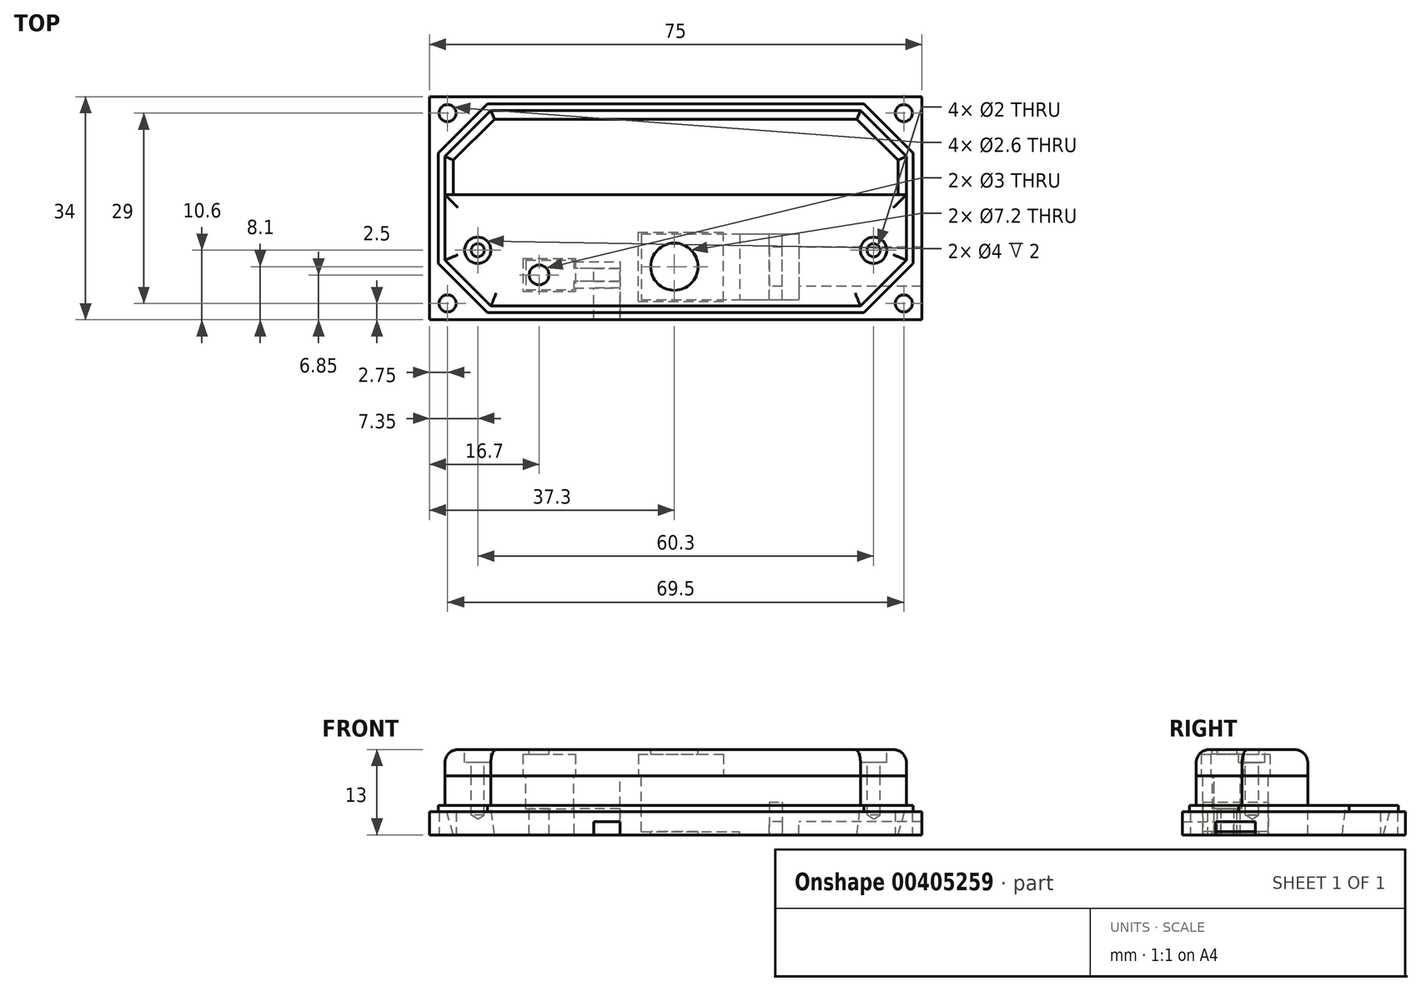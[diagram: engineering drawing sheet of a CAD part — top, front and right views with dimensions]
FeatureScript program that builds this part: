
annotation { "Feature Type Name" : "Feature", "Feature Type Description" : "" }
export const myFeature = defineFeature(function(context is Context, id is Id, definition is map)
    precondition{}
    {
        {
            var Q0;
            Q0=qCreatedBy(makeId("Top.planeOp"),FACE);
            var sketch = newSketch(context, id + "F0", { "sketchPlane" : qUnion([Q0])});
            skLineSegment(sketch, "E0.bottom", {"start": v(37.5, -17) * mm, "end": v(-37.5, -17) * mm});
            skLineSegment(sketch, "E0.top", {"start": v(37.5, 17) * mm, "end": v(-37.5, 17) * mm});
            skLineSegment(sketch, "E0.left", {"start": v(37.5, -17) * mm, "end": v(37.5, 17) * mm});
            skLineSegment(sketch, "E0.right", {"start": v(-37.5, -17) * mm, "end": v(-37.5, 17) * mm});
            skPoint(sketch, "E0.middle", {"position": v(0, 0) * mm});
            skLineSegment(sketch, "E1.bottom", {"start": v(-28.65, 15.9) * mm, "end": v(28.65, 15.9) * mm, "construction": true});
            skLineSegment(sketch, "E1.top", {"start": v(-28.65, -15.9) * mm, "end": v(28.65, -15.9) * mm, "construction": true});
            skLineSegment(sketch, "E1.left", {"start": v(-36.15, 8.4) * mm, "end": v(-36.15, -8.4) * mm, "construction": true});
            skLineSegment(sketch, "E1.right", {"start": v(36.15, 8.4) * mm, "end": v(36.15, -8.4) * mm, "construction": true});
            skLineSegment(sketch, "E2", {"start": v(-36.15, 8.4) * mm, "end": v(-28.65, 15.9) * mm, "construction": true});
            skLineSegment(sketch, "E3", {"start": v(28.65, 15.9) * mm, "end": v(36.15, 8.4) * mm, "construction": true});
            skLineSegment(sketch, "E4", {"start": v(36.15, -8.4) * mm, "end": v(28.65, -15.9) * mm, "construction": true});
            skLineSegment(sketch, "E5", {"start": v(-36.15, -8.4) * mm, "end": v(-28.65, -15.9) * mm, "construction": true});
            skCircle(sketch, "E6", {"center": v(-34.75, 14.5) * mm, "radius": 1.3 * mm});
            skCircle(sketch, "E7", {"center": v(34.75, 14.5) * mm, "radius": 1.3 * mm});
            skCircle(sketch, "E8", {"center": v(-34.75, -14.5) * mm, "radius": 1.3 * mm});
            skCircle(sketch, "E9", {"center": v(34.75, -14.5) * mm, "radius": 1.3 * mm});
            skLineSegment(sketch, "E10", {"start": v(0, -47.1) * mm, "end": v(0, -78.86) * mm, "construction": true});
            skSolve(sketch);
        }
        {
            var Q0;
            Q0=qSketchRegion(id+"F0",true);
            extrude(context, id + "F1", {"entities" : qUnion([Q0]), "depth" : 3.5 * mm});
        }
        {
            var Q0;
            Q0=makeQuery(id+"F1.opExtrude","CAP_FACE",FACE,{"disambiguationData":[OSD([sQuery(id+"F0.wireOp",EDGE,"E0.bottom"),sQuery(id+"F0.wireOp",EDGE,"E0.top"),sQuery(id+"F0.wireOp",EDGE,"E0.left"),sQuery(id+"F0.wireOp",EDGE,"E0.right"),sQuery(id+"F0.wireOp",EDGE,"E6"),sQuery(id+"F0.wireOp",EDGE,"E7"),sQuery(id+"F0.wireOp",EDGE,"E8"),sQuery(id+"F0.wireOp",EDGE,"E9")])],"isStart":false});
            var sketch = newSketch(context, id + "F2", { "sketchPlane" : qUnion([Q0])});
            skLineSegment(sketch, "E11.bottom", {"start": v(-28.65, 15.9) * mm, "end": v(28.65, 15.9) * mm});
            skLineSegment(sketch, "E11.top", {"start": v(-28.65, -15.9) * mm, "end": v(28.65, -15.9) * mm});
            skLineSegment(sketch, "E11.left", {"start": v(-36.15, 8.4) * mm, "end": v(-36.15, -8.4) * mm});
            skLineSegment(sketch, "E11.right", {"start": v(36.15, 8.4) * mm, "end": v(36.15, -8.4) * mm});
            skLineSegment(sketch, "E12", {"start": v(-36.15, 8.4) * mm, "end": v(-28.65, 15.9) * mm});
            skLineSegment(sketch, "E13", {"start": v(28.65, 15.9) * mm, "end": v(36.15, 8.4) * mm});
            skLineSegment(sketch, "E14", {"start": v(36.15, -8.4) * mm, "end": v(28.65, -15.9) * mm});
            skLineSegment(sketch, "E15", {"start": v(-36.15, -8.4) * mm, "end": v(-28.65, -15.9) * mm});
            skSolve(sketch);
        }
        {
            var Q0;
            Q0=qSketchRegion(id+"F2",true);
            extrude(context, id + "F3", {"entities" : qUnion([Q0]), "operationType" : NewBodyOperationType.ADD, "depth" : 1 * mm});
        }
        {
            var Q0;
            Q0=makeQuery(id+"F3.opExtrude","CAP_FACE",FACE,{"disambiguationData":[OSD([sQuery(id+"F2.wireOp",EDGE,"E11.bottom"),sQuery(id+"F2.wireOp",EDGE,"E11.top"),sQuery(id+"F2.wireOp",EDGE,"E11.left"),sQuery(id+"F2.wireOp",EDGE,"E11.right"),sQuery(id+"F2.wireOp",EDGE,"E12"),sQuery(id+"F2.wireOp",EDGE,"E13"),sQuery(id+"F2.wireOp",EDGE,"E14"),sQuery(id+"F2.wireOp",EDGE,"E15")])],"isStart":false});
            var sketch = newSketch(context, id + "F4", { "sketchPlane" : qUnion([Q0])});
            skLineSegment(sketch, "E16.bottom", {"start": v(-28.15, 14.9) * mm, "end": v(28.15, 14.9) * mm});
            skLineSegment(sketch, "E16.top", {"start": v(-28.15, -14.9) * mm, "end": v(28.15, -14.9) * mm});
            skLineSegment(sketch, "E16.left", {"start": v(-35.15, 7.9) * mm, "end": v(-35.15, -7.9) * mm});
            skLineSegment(sketch, "E16.right", {"start": v(35.15, 7.9) * mm, "end": v(35.15, -7.9) * mm});
            skLineSegment(sketch, "E17", {"start": v(-35.15, 7.9) * mm, "end": v(-28.15, 14.9) * mm});
            skLineSegment(sketch, "E18", {"start": v(28.15, 14.9) * mm, "end": v(35.15, 7.9) * mm});
            skLineSegment(sketch, "E19", {"start": v(35.15, -7.9) * mm, "end": v(28.15, -14.9) * mm});
            skLineSegment(sketch, "E20", {"start": v(-35.15, -7.9) * mm, "end": v(-28.15, -14.9) * mm});
            skSolve(sketch);
        }
        {
            var Q0;
            Q0=qSketchRegion(id+"F4",true);
            extrude(context, id + "F5", {"entities" : qUnion([Q0]), "operationType" : NewBodyOperationType.REMOVE, "oppositeDirection" : true, "depth" : 5 * mm});
        }
        {
            var Q0;
            Q0=qCreatedBy(makeId("Front.planeOp"),FACE);
            cPlane(context, id + "F6", {"entities" : qUnion([Q0]), "cplaneType" : CPlaneType.OFFSET, "offset" : 2.1 * mm, "oppositeDirection" : true, "width" : 150 * mm, "height" : 150 * mm});
        }
        {
            var Q0;
            Q0=qCreatedBy(id+"F6.planeOp",FACE);
            var sketch = newSketch(context, id + "F7", { "sketchPlane" : qUnion([Q0])});
            skLineSegment(sketch, "E21", {"start": v(-35.15, 4.5) * mm, "end": v(-35.15, 0) * mm});
            skLineSegment(sketch, "E22", {"start": v(-33.85, 0) * mm, "end": v(-35.15, 0) * mm});
            skLineSegment(sketch, "E23", {"start": v(-33.85, 0) * mm, "end": v(-35.15, 4.5) * mm});
            skSolve(sketch);
        }
        {
            var Q0;
            Q0=makeQuery(id+"F3.opExtrude","CAP_FACE",FACE,{"disambiguationData":[OSD([sQuery(id+"F2.wireOp",EDGE,"E11.bottom"),sQuery(id+"F2.wireOp",EDGE,"E11.top"),sQuery(id+"F2.wireOp",EDGE,"E11.left"),sQuery(id+"F2.wireOp",EDGE,"E11.right"),sQuery(id+"F2.wireOp",EDGE,"E12"),sQuery(id+"F2.wireOp",EDGE,"E13"),sQuery(id+"F2.wireOp",EDGE,"E14"),sQuery(id+"F2.wireOp",EDGE,"E15")])],"isStart":false});
            var sketch = newSketch(context, id + "F8", { "sketchPlane" : qUnion([Q0])});
            skLineSegment(sketch, "E24.bottom", {"start": v(-28.15, 14.9) * mm, "end": v(28.15, 14.9) * mm});
            skLineSegment(sketch, "E24.left", {"start": v(-35.15, 7.9) * mm, "end": v(-35.15, 2.1) * mm});
            skLineSegment(sketch, "E24.right", {"start": v(35.15, 7.9) * mm, "end": v(35.15, 2.1) * mm});
            skLineSegment(sketch, "E25", {"start": v(-35.15, 7.9) * mm, "end": v(-28.15, 14.9) * mm});
            skLineSegment(sketch, "E26", {"start": v(28.15, 14.9) * mm, "end": v(35.15, 7.9) * mm});
            skSolve(sketch);
        }
        {
            var Q0;
            Q0=qSketchRegion(id+"F7",true);
            var Q1;
            Q1=qConstructionFilter(qBodyType(qCreatedBy(id+"F8",EDGE),BodyType.WIRE),ConstructionObject.NO);
            sweep(context, id + "F9", {"operationType" : NewBodyOperationType.ADD, "profiles" : qUnion([Q0]), "path" : qUnion([Q1])});
        }
        {
            var Q0;
            Q0=qCreatedBy(makeId("Top.planeOp"),FACE);
            var sketch = newSketch(context, id + "F10", { "sketchPlane" : qUnion([Q0])});
            skLineSegment(sketch, "E27.top", {"start": v(-28.15, -14.9) * mm, "end": v(28.15, -14.9) * mm});
            skLineSegment(sketch, "E27.left", {"start": v(-35.15, 2.1) * mm, "end": v(-35.15, -7.9) * mm});
            skLineSegment(sketch, "E27.right", {"start": v(35.15, 2.1) * mm, "end": v(35.15, -7.9) * mm});
            skLineSegment(sketch, "E28", {"start": v(35.15, -7.9) * mm, "end": v(28.15, -14.9) * mm});
            skLineSegment(sketch, "E29", {"start": v(-35.15, -7.9) * mm, "end": v(-28.15, -14.9) * mm});
            skLineSegment(sketch, "E30", {"start": v(-35.15, 2.1) * mm, "end": v(35.15, 2.1) * mm});
            skSolve(sketch);
        }
        {
            var Q0;
            Q0=qSketchRegion(id+"F10",true);
            extrude(context, id + "F11", {"entities" : qUnion([Q0]), "operationType" : NewBodyOperationType.ADD, "depth" : 9 * mm});
        }
        {
            var Q0;
            Q0=makeQuery(id+"F11.opExtrude","CAP_FACE",FACE,{"disambiguationData":[OSD([sQuery(id+"F10.wireOp",EDGE,"E27.top"),sQuery(id+"F10.wireOp",EDGE,"E27.left"),sQuery(id+"F10.wireOp",EDGE,"E27.right"),sQuery(id+"F10.wireOp",EDGE,"E28"),sQuery(id+"F10.wireOp",EDGE,"E29"),sQuery(id+"F10.wireOp",EDGE,"E30")])],"isStart":false});
            var sketch = newSketch(context, id + "F12", { "sketchPlane" : qUnion([Q0])});
            skLineSegment(sketch, "E31.bottom", {"start": v(-5.25, -3.9) * mm, "end": v(9.75, -3.9) * mm});
            skLineSegment(sketch, "E31.top", {"start": v(-5.25, -13.9) * mm, "end": v(9.75, -13.9) * mm});
            skLineSegment(sketch, "E31.left", {"start": v(-5.25, -3.9) * mm, "end": v(-5.25, -13.9) * mm});
            skLineSegment(sketch, "E31.right", {"start": v(9.75, -3.9) * mm, "end": v(9.75, -13.9) * mm});
            skSolve(sketch);
        }
        {
            var Q0;
            Q0=qSketchRegion(id+"F12",true);
            extrude(context, id + "F13", {"entities" : qUnion([Q0]), "operationType" : NewBodyOperationType.REMOVE, "oppositeDirection" : true, "depth" : 8.5 * mm});
        }
        {
            var Q0;
            Q0=makeQuery(id+"F11.opExtrude","CAP_FACE",FACE,{"disambiguationData":[OSD([sQuery(id+"F10.wireOp",EDGE,"E27.top"),sQuery(id+"F10.wireOp",EDGE,"E27.left"),sQuery(id+"F10.wireOp",EDGE,"E27.right"),sQuery(id+"F10.wireOp",EDGE,"E28"),sQuery(id+"F10.wireOp",EDGE,"E29"),sQuery(id+"F10.wireOp",EDGE,"E30")])],"isStart":false});
            var sketch = newSketch(context, id + "F14", { "sketchPlane" : qUnion([Q0])});
            skLineSegment(sketch, "E32.bottom", {"start": v(-22.8, -7.9) * mm, "end": v(-15.5, -7.9) * mm});
            skLineSegment(sketch, "E32.top", {"start": v(-22.8, -12.4) * mm, "end": v(-15.5, -12.4) * mm});
            skLineSegment(sketch, "E32.left", {"start": v(-22.8, -7.9) * mm, "end": v(-22.8, -12.4) * mm});
            skLineSegment(sketch, "E32.right", {"start": v(-15.5, -7.9) * mm, "end": v(-15.5, -12.4) * mm});
            skSolve(sketch);
        }
        {
            var Q0;
            Q0=qSketchRegion(id+"F14",true);
            extrude(context, id + "F15", {"entities" : qUnion([Q0]), "operationType" : NewBodyOperationType.REMOVE, "oppositeDirection" : true, "depth" : 5 * mm});
        }
        {
            var Q0;
            Q0=makeQuery(id+"F11.opExtrude","CAP_FACE",FACE,{"disambiguationData":[OSD([sQuery(id+"F10.wireOp",EDGE,"E27.top"),sQuery(id+"F10.wireOp",EDGE,"E27.left"),sQuery(id+"F10.wireOp",EDGE,"E27.right"),sQuery(id+"F10.wireOp",EDGE,"E28"),sQuery(id+"F10.wireOp",EDGE,"E29"),sQuery(id+"F10.wireOp",EDGE,"E30")])],"isStart":false});
            var sketch = newSketch(context, id + "F16", { "sketchPlane" : qUnion([Q0])});
            skLineSegment(sketch, "E33.bottom", {"start": v(9.75, -3.9) * mm, "end": v(18.75, -3.9) * mm});
            skLineSegment(sketch, "E33.top", {"start": v(9.75, -13.9) * mm, "end": v(18.75, -13.9) * mm});
            skLineSegment(sketch, "E33.left", {"start": v(9.75, -3.9) * mm, "end": v(9.75, -13.9) * mm});
            skLineSegment(sketch, "E33.right", {"start": v(18.75, -3.9) * mm, "end": v(18.75, -13.9) * mm});
            skLineSegment(sketch, "E34.bottom", {"start": v(-15.5, -8.15) * mm, "end": v(-8.5, -8.15) * mm});
            skLineSegment(sketch, "E34.top", {"start": v(-15.5, -12.15) * mm, "end": v(-8.5, -12.15) * mm});
            skLineSegment(sketch, "E34.left", {"start": v(-15.5, -8.15) * mm, "end": v(-15.5, -12.15) * mm});
            skLineSegment(sketch, "E34.right", {"start": v(-8.5, -8.15) * mm, "end": v(-8.5, -12.15) * mm});
            skSolve(sketch);
        }
        {
            var Q0;
            Q0=qSketchRegion(id+"F16",true);
            extrude(context, id + "F17", {"entities" : qUnion([Q0]), "operationType" : NewBodyOperationType.REMOVE, "oppositeDirection" : true, "depth" : 25 * mm});
        }
        {
            var Q0;
            Q0=makeQuery(id+"F17.boolean.opBoolean","MERGE",FACE,{"derivedFrom":[makeQuery(id+"F13.boolean.opBoolean","COPY",FACE,{"derivedFrom":makeQuery(id+"F13.opExtrude","SWEPT_FACE",FACE,{"disambiguationData":[OSD([sQuery(id+"F12.wireOp",EDGE,"E31.bottom")])]})}),makeQuery(id+"F17.opExtrude","SWEPT_FACE",FACE,{"disambiguationData":[OSD([sQuery(id+"F16.wireOp",EDGE,"E33.bottom")])]})]});
            var sketch = newSketch(context, id + "F18", { "sketchPlane" : qUnion([Q0])});
            skLineSegment(sketch, "E35.bottom", {"start": v(14.25, 5) * mm, "end": v(16.25, 5) * mm});
            skLineSegment(sketch, "E35.top", {"start": v(14.25, 0) * mm, "end": v(16.25, 0) * mm});
            skLineSegment(sketch, "E35.left", {"start": v(14.25, 5) * mm, "end": v(14.25, 0) * mm});
            skLineSegment(sketch, "E35.right", {"start": v(16.25, 5) * mm, "end": v(16.25, 0) * mm});
            skSolve(sketch);
        }
        {
            var Q0;
            Q0=qSketchRegion(id+"F18",true);
            extrude(context, id + "F19", {"entities" : qUnion([Q0]), "operationType" : NewBodyOperationType.ADD, "depth" : 10 * mm});
        }
        {
            var Q0;
            Q0=makeQuery(id+"F19.opExtrude","SWEPT_FACE",FACE,{"disambiguationData":[OSD([sQuery(id+"F18.wireOp",EDGE,"E35.left")])]});
            var sketch = newSketch(context, id + "F20", { "sketchPlane" : qUnion([Q0])});
            skLineSegment(sketch, "E36.bottom", {"start": v(5.9, 0) * mm, "end": v(11.9, 0) * mm});
            skLineSegment(sketch, "E36.top", {"start": v(5.9, 2) * mm, "end": v(11.9, 2) * mm});
            skLineSegment(sketch, "E36.left", {"start": v(5.9, 0) * mm, "end": v(5.9, 2) * mm});
            skLineSegment(sketch, "E36.right", {"start": v(11.9, 0) * mm, "end": v(11.9, 2) * mm});
            skSolve(sketch);
        }
        {
            var Q0;
            Q0=qSketchRegion(id+"F20",true);
            extrude(context, id + "F21", {"entities" : qUnion([Q0]), "operationType" : NewBodyOperationType.REMOVE, "oppositeDirection" : true, "depth" : 25 * mm});
        }
        {
            var Q0;
            Q0=makeQuery(id+"F11.opExtrude","CAP_FACE",FACE,{"disambiguationData":[OSD([sQuery(id+"F10.wireOp",EDGE,"E27.top"),sQuery(id+"F10.wireOp",EDGE,"E27.left"),sQuery(id+"F10.wireOp",EDGE,"E27.right"),sQuery(id+"F10.wireOp",EDGE,"E28"),sQuery(id+"F10.wireOp",EDGE,"E29"),sQuery(id+"F10.wireOp",EDGE,"E30")])],"isStart":false});
            var sketch = newSketch(context, id + "F22", { "sketchPlane" : qUnion([Q0])});
            skCircle(sketch, "E37", {"center": v(-30.15, -6.4) * mm, "radius": 0.8 * mm});
            skCircle(sketch, "E38", {"center": v(30.15, -6.4) * mm, "radius": 0.8 * mm});
            skSolve(sketch);
        }
        {
            var Q0;
            Q0=qSketchRegion(id+"F22",true);
            extrude(context, id + "F23", {"entities" : qUnion([Q0]), "operationType" : NewBodyOperationType.REMOVE, "oppositeDirection" : true, "depth" : 5 * mm});
        }
        {
            var Q0;
            Q0=qCreatedBy(makeId("Top.planeOp"),FACE);
            cPlane(context, id + "F24", {"entities" : qUnion([Q0]), "cplaneType" : CPlaneType.OFFSET, "offset" : 9 * mm, "width" : 150 * mm, "height" : 150 * mm});
        }
        {
            var Q0;
            Q0=qCreatedBy(id+"F24.planeOp",FACE);
            var sketch = newSketch(context, id + "F25", { "sketchPlane" : qUnion([Q0])});
            skLineSegment(sketch, "E39.top", {"start": v(-28.15, -14.9) * mm, "end": v(28.15, -14.9) * mm});
            skLineSegment(sketch, "E39.left", {"start": v(-35.15, 2.1) * mm, "end": v(-35.15, -7.9) * mm});
            skLineSegment(sketch, "E39.right", {"start": v(35.15, 2.1) * mm, "end": v(35.15, -7.9) * mm});
            skLineSegment(sketch, "E40", {"start": v(35.15, -7.9) * mm, "end": v(28.15, -14.9) * mm});
            skLineSegment(sketch, "E41", {"start": v(-35.15, -7.9) * mm, "end": v(-28.15, -14.9) * mm});
            skLineSegment(sketch, "E42", {"start": v(-35.15, 2.1) * mm, "end": v(35.15, 2.1) * mm});
            skSolve(sketch);
        }
        {
            var Q0;
            Q0=qSketchRegion(id+"F25",true);
            extrude(context, id + "F26", {"entities" : qUnion([Q0]), "depth" : 4 * mm});
        }
        {
            var Q0;
            Q0=makeQuery(id+"F26.opExtrude","CAP_FACE",FACE,{"disambiguationData":[OSD([sQuery(id+"F25.wireOp",EDGE,"E39.top"),sQuery(id+"F25.wireOp",EDGE,"E39.left"),sQuery(id+"F25.wireOp",EDGE,"E39.right"),sQuery(id+"F25.wireOp",EDGE,"E40"),sQuery(id+"F25.wireOp",EDGE,"E41"),sQuery(id+"F25.wireOp",EDGE,"E42")])],"isStart":false});
            var sketch = newSketch(context, id + "F27", { "sketchPlane" : qUnion([Q0])});
            skCircle(sketch, "E43", {"center": v(-0.2, -8.9) * mm, "radius": 3.6 * mm});
            skCircle(sketch, "E44", {"center": v(-20.8, -10.15) * mm, "radius": 1.5 * mm});
            skSolve(sketch);
        }
        {
            var Q0;
            Q0=qSketchRegion(id+"F27",true);
            extrude(context, id + "F28", {"entities" : qUnion([Q0]), "operationType" : NewBodyOperationType.REMOVE, "oppositeDirection" : true, "depth" : 25 * mm});
        }
        {
            var Q0;
            Q0=makeQuery(id+"F26.opExtrude","CAP_FACE",FACE,{"disambiguationData":[OSD([sQuery(id+"F25.wireOp",EDGE,"E39.top"),sQuery(id+"F25.wireOp",EDGE,"E39.left"),sQuery(id+"F25.wireOp",EDGE,"E39.right"),sQuery(id+"F25.wireOp",EDGE,"E40"),sQuery(id+"F25.wireOp",EDGE,"E41"),sQuery(id+"F25.wireOp",EDGE,"E42")])],"isStart":true});
            var sketch = newSketch(context, id + "F29", { "sketchPlane" : qUnion([Q0])});
            skLineSegment(sketch, "E45.bottom", {"start": v(-5.7, 14.15) * mm, "end": v(7.3, 14.15) * mm});
            skLineSegment(sketch, "E45.top", {"start": v(-5.7, 3.65) * mm, "end": v(7.3, 3.65) * mm});
            skLineSegment(sketch, "E45.left", {"start": v(-5.7, 14.15) * mm, "end": v(-5.7, 3.65) * mm});
            skLineSegment(sketch, "E45.right", {"start": v(7.3, 14.15) * mm, "end": v(7.3, 3.65) * mm});
            skPoint(sketch, "E45.middle", {"position": v(0.8, 8.9) * mm});
            skLineSegment(sketch, "E46.bottom", {"start": v(-23.3, 7.65) * mm, "end": v(-15.3, 7.65) * mm});
            skLineSegment(sketch, "E46.top", {"start": v(-23.3, 12.65) * mm, "end": v(-15.3, 12.65) * mm});
            skLineSegment(sketch, "E46.left", {"start": v(-23.3, 7.65) * mm, "end": v(-23.3, 12.65) * mm});
            skLineSegment(sketch, "E46.right", {"start": v(-15.3, 7.65) * mm, "end": v(-15.3, 12.65) * mm});
            skCircle(sketch, "E47", {"center": v(-20.8, 10.15) * mm, "radius": 1.5 * mm, "construction": true});
            skSolve(sketch);
        }
        {
            var Q0;
            Q0=qSketchRegion(id+"F29",true);
            extrude(context, id + "F30", {"entities" : qUnion([Q0]), "operationType" : NewBodyOperationType.REMOVE, "oppositeDirection" : true, "depth" : 3.3 * mm});
        }
        {
            var Q0;
            Q0=makeQuery(id+"F17.boolean.opBoolean","COPY",FACE,{"derivedFrom":makeQuery(id+"F17.opExtrude","SWEPT_FACE",FACE,{"disambiguationData":[OSD([sQuery(id+"F16.wireOp",EDGE,"E34.left")])]})});
            var sketch = newSketch(context, id + "F31", { "sketchPlane" : qUnion([Q0])});
            skLineSegment(sketch, "E48.bottom", {"start": v(-11.15, 4) * mm, "end": v(-9.15, 4) * mm});
            skLineSegment(sketch, "E48.top", {"start": v(-11.15, 0) * mm, "end": v(-9.15, 0) * mm});
            skLineSegment(sketch, "E48.left", {"start": v(-11.15, 4) * mm, "end": v(-11.15, 0) * mm});
            skLineSegment(sketch, "E48.right", {"start": v(-9.15, 4) * mm, "end": v(-9.15, 0) * mm});
            skSolve(sketch);
        }
        {
            var Q0;
            Q0=qSketchRegion(id+"F31",true);
            extrude(context, id + "F32", {"entities" : qUnion([Q0]), "operationType" : NewBodyOperationType.ADD, "depth" : 7 * mm});
        }
        {
            var Q0;
            Q0=makeQuery(id+"F32.opExtrude","SWEPT_FACE",FACE,{"disambiguationData":[OSD([sQuery(id+"F31.wireOp",EDGE,"E48.right")])]});
            var sketch = newSketch(context, id + "F33", { "sketchPlane" : qUnion([Q0])});
            skLineSegment(sketch, "E49.bottom", {"start": v(12.5, 0) * mm, "end": v(8.5, 0) * mm});
            skLineSegment(sketch, "E49.top", {"start": v(12.5, 2) * mm, "end": v(8.5, 2) * mm});
            skLineSegment(sketch, "E49.left", {"start": v(12.5, 0) * mm, "end": v(12.5, 2) * mm});
            skLineSegment(sketch, "E49.right", {"start": v(8.5, 0) * mm, "end": v(8.5, 2) * mm});
            skSolve(sketch);
        }
        {
            var Q0;
            Q0=qSketchRegion(id+"F33",true);
            extrude(context, id + "F34", {"entities" : qUnion([Q0]), "operationType" : NewBodyOperationType.REMOVE, "oppositeDirection" : true, "depth" : 25 * mm});
        }
        {
            var Q0;
            Q0=makeQuery(id+"F26.opExtrude","CAP_FACE",FACE,{"disambiguationData":[OSD([sQuery(id+"F25.wireOp",EDGE,"E39.top"),sQuery(id+"F25.wireOp",EDGE,"E39.left"),sQuery(id+"F25.wireOp",EDGE,"E39.right"),sQuery(id+"F25.wireOp",EDGE,"E40"),sQuery(id+"F25.wireOp",EDGE,"E41"),sQuery(id+"F25.wireOp",EDGE,"E42")])],"isStart":false});
            var sketch = newSketch(context, id + "F35", { "sketchPlane" : qUnion([Q0])});
            skCircle(sketch, "E50", {"center": v(-30.15, -6.4) * mm, "radius": 1 * mm, "construction": true});
            skCircle(sketch, "E51", {"center": v(30.15, -6.4) * mm, "radius": 1 * mm, "construction": true});
            skSolve(sketch);
        }
        {
            var Q0;
            Q0=sQuery(id+"F35.wireOp",VERTEX,"E50.center");
            var Q1;
            Q1=sQuery(id+"F35.wireOp",VERTEX,"E51.center");
            var Q2;
            Q2=makeQuery(id+"F1.opExtrude","SWEPT_BODY",BODY,{"disambiguationData":[OSD([sQuery(id+"F0.wireOp",EDGE,"E0.bottom"),sQuery(id+"F0.wireOp",EDGE,"E0.top"),sQuery(id+"F0.wireOp",EDGE,"E0.left"),sQuery(id+"F0.wireOp",EDGE,"E0.right"),sQuery(id+"F0.wireOp",EDGE,"E6"),sQuery(id+"F0.wireOp",EDGE,"E7"),sQuery(id+"F0.wireOp",EDGE,"E8"),sQuery(id+"F0.wireOp",EDGE,"E9")])]});
            var Q3;
            Q3=makeQuery(id+"F26.opExtrude","SWEPT_BODY",BODY,{"disambiguationData":[OSD([sQuery(id+"F25.wireOp",EDGE,"E39.top"),sQuery(id+"F25.wireOp",EDGE,"E39.left"),sQuery(id+"F25.wireOp",EDGE,"E39.right"),sQuery(id+"F25.wireOp",EDGE,"E40"),sQuery(id+"F25.wireOp",EDGE,"E41"),sQuery(id+"F25.wireOp",EDGE,"E42")])]});
            hole(context, id + "F36", {"style" : HoleStyle.C_BORE, "endStyle" : HoleEndStyle.BLIND, "holeDiameter" : 2 * mm, "cBoreDiameter" : 4 * mm, "cBoreDepth" : 2 * mm, "holeDepth" : 10 * mm, "tappedDepth" : 12 * mm, "tapClearance" : 3, "locations" : qUnion([Q0, Q1]), "scope" : qUnion([Q2, Q3])});
        }
        {
            var Q0;
            Q0=makeQuery(id+"F26.opExtrude","CAP_EDGE",EDGE,{"disambiguationData":[OSD([sQuery(id+"F25.wireOp",EDGE,"E39.top")])],"isStart":false});
            var Q1;
            Q1=makeQuery(id+"F26.opExtrude","CAP_EDGE",EDGE,{"disambiguationData":[OSD([sQuery(id+"F25.wireOp",EDGE,"E41")])],"isStart":false});
            var Q2;
            Q2=makeQuery(id+"F26.opExtrude","CAP_EDGE",EDGE,{"disambiguationData":[OSD([sQuery(id+"F25.wireOp",EDGE,"E39.left")])],"isStart":false});
            var Q3;
            Q3=makeQuery(id+"F26.opExtrude","CAP_EDGE",EDGE,{"disambiguationData":[OSD([sQuery(id+"F25.wireOp",EDGE,"E42")])],"isStart":false});
            var Q4;
            Q4=makeQuery(id+"F26.opExtrude","CAP_EDGE",EDGE,{"disambiguationData":[OSD([sQuery(id+"F25.wireOp",EDGE,"E39.right")])],"isStart":false});
            var Q5;
            Q5=makeQuery(id+"F26.opExtrude","CAP_EDGE",EDGE,{"disambiguationData":[OSD([sQuery(id+"F25.wireOp",EDGE,"E40")])],"isStart":false});
            fillet(context, id + "F37", {"entities" : qUnion([Q0, Q1, Q2, Q3, Q4, Q5]), "radius" : 2 * mm, "tangentPropagation" : true, "allowEdgeOverflow" : false});
        }
    });
